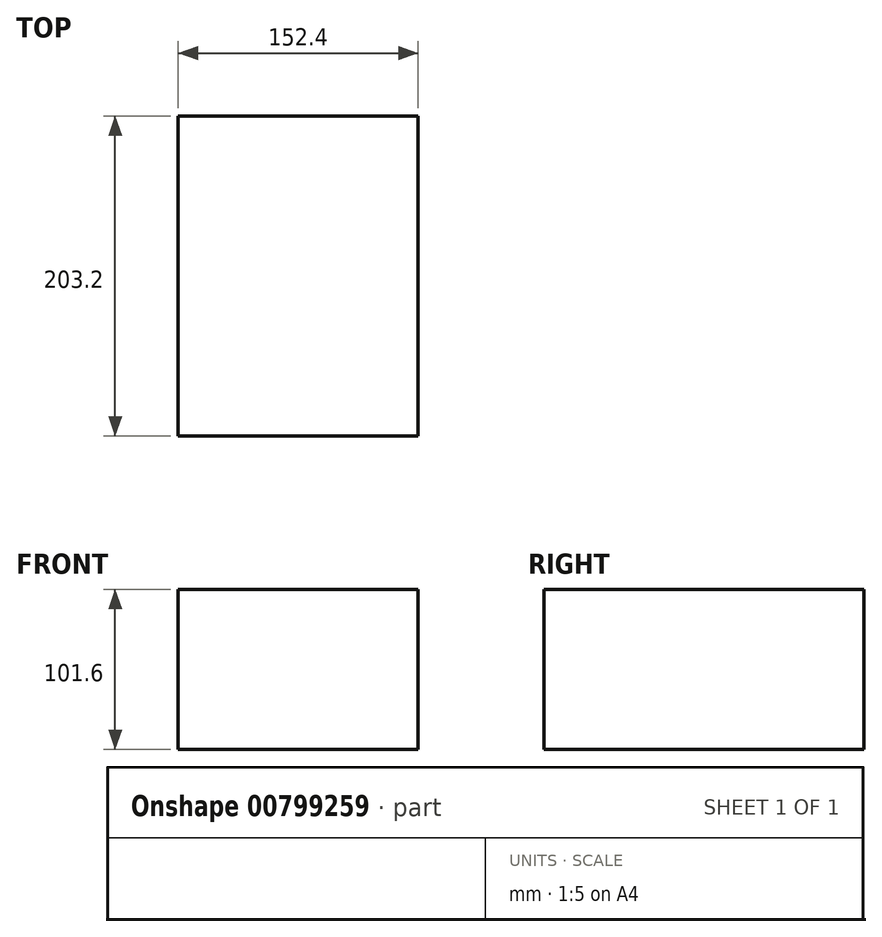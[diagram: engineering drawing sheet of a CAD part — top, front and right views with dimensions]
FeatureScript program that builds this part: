
annotation { "Feature Type Name" : "Feature", "Feature Type Description" : "" }
export const myFeature = defineFeature(function(context is Context, id is Id, definition is map)
    precondition{}
    {
        {
            var Q0;
            Q0=qCreatedBy(makeId("Top.planeOp"),FACE);
            var sketch = newSketch(context, id + "F0", { "sketchPlane" : qUnion([Q0])});
            skLineSegment(sketch, "E0.bottom", {"start": v(-37.7, -15.99) * mm, "end": v(114.7, -15.99) * mm});
            skLineSegment(sketch, "E0.top", {"start": v(-37.7, 187.21) * mm, "end": v(114.7, 187.21) * mm});
            skLineSegment(sketch, "E0.left", {"start": v(-37.7, -15.99) * mm, "end": v(-37.7, 187.21) * mm});
            skLineSegment(sketch, "E0.right", {"start": v(114.7, -15.99) * mm, "end": v(114.7, 187.21) * mm});
            skSolve(sketch);
        }
        {
            var Q0;
            Q0=makeQuery(id+"F0.imprint","IMPRINT",FACE,{"disambiguationData":[TD([[makeQuery(id+"F0.imprint","IMPRINT",EDGE,{"derivedFrom":sQuery(id+"F0.wireOp",EDGE,"E0.bottom")}),1.0]])]});
            extrude(context, id + "F1", {"entities" : qUnion([Q0]), "depth" : 101.6 * mm, "offsetDistance" : 25.4 * mm});
        }
    });
